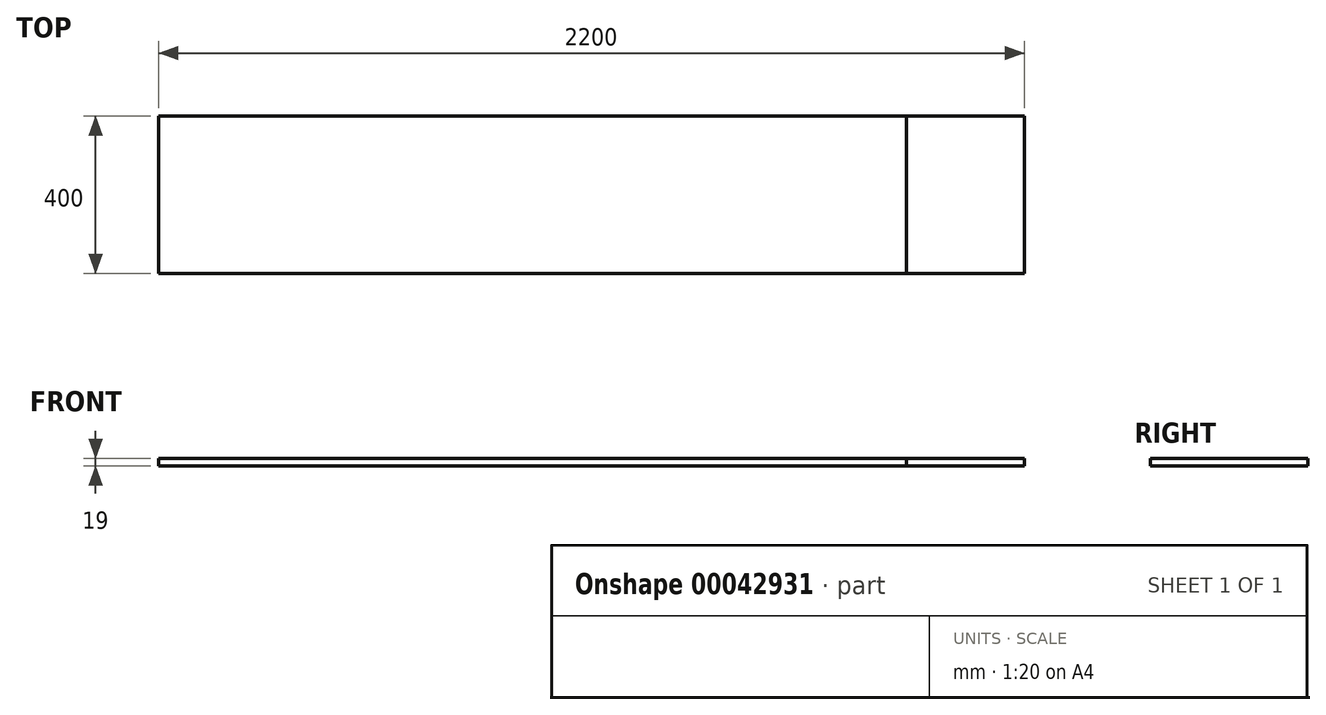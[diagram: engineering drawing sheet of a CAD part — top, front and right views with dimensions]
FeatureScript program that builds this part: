
annotation { "Feature Type Name" : "Feature", "Feature Type Description" : "" }
export const myFeature = defineFeature(function(context is Context, id is Id, definition is map)
    precondition{}
    {
        {
            var Q0;
            Q0=qCreatedBy(makeId("Right.planeOp"),FACE);
            var sketch = newSketch(context, id + "F0", { "sketchPlane" : qUnion([Q0])});
            skLineSegment(sketch, "E0.bottom", {"start": v(0, 0) * mm, "end": v(400, 0) * mm});
            skLineSegment(sketch, "E0.top", {"start": v(0, 19) * mm, "end": v(400, 19) * mm});
            skLineSegment(sketch, "E0.left", {"start": v(0, 0) * mm, "end": v(0, 19) * mm});
            skLineSegment(sketch, "E0.right", {"start": v(400, 0) * mm, "end": v(400, 19) * mm});
            skSolve(sketch);
        }
        {
            var Q0;
            Q0=makeQuery(id+"F0.imprint","IMPRINT",FACE,{"disambiguationData":[TD([[makeQuery(id+"F0.imprint","IMPRINT",EDGE,{"derivedFrom":sQuery(id+"F0.wireOp",EDGE,"E0.bottom")}),1.0]])]});
            extrude(context, id + "F1", {"entities" : qUnion([Q0]), "depth" : 2200 * mm});
        }
        {
            var Q0;
            Q0 = qSketchRegion(id + "F0", true);
            extrude(context, id + "F2", {"entities" : qUnion([Q0]), "depth" : 1900 * mm});
        }
    });
